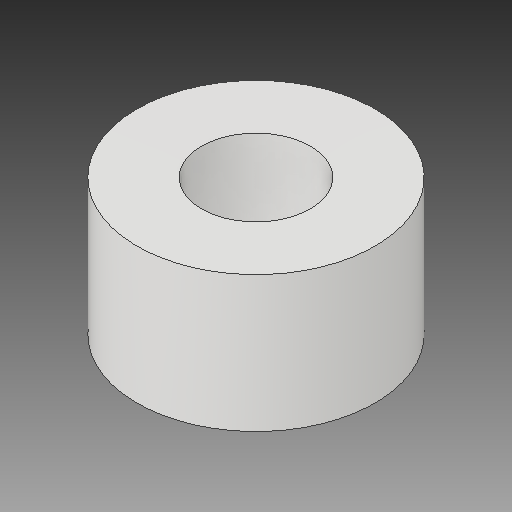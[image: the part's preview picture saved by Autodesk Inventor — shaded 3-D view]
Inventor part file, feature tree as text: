
AUTODESK INVENTOR PART (.ipt)
format: ipt  version: 2018.2 (Build 222227000, 227)  size: 96,256 bytes
history: native  units: mm
features: extrude x1, sketch x1
ambient origin geometry x8: Origin, YZ Plane, XZ Plane, XY Plane, X Axis, Y Axis, Z Axis, Center Point
bodies: Solid1 (feature_tree)
feature tree (2):
  extrude  "Extrusion1"  Depth=4.0mm
  sketch  "Sketch1"  dims[d0=3.2mm d1=7.0mm d2=4.0mm d3=0.0mm]
